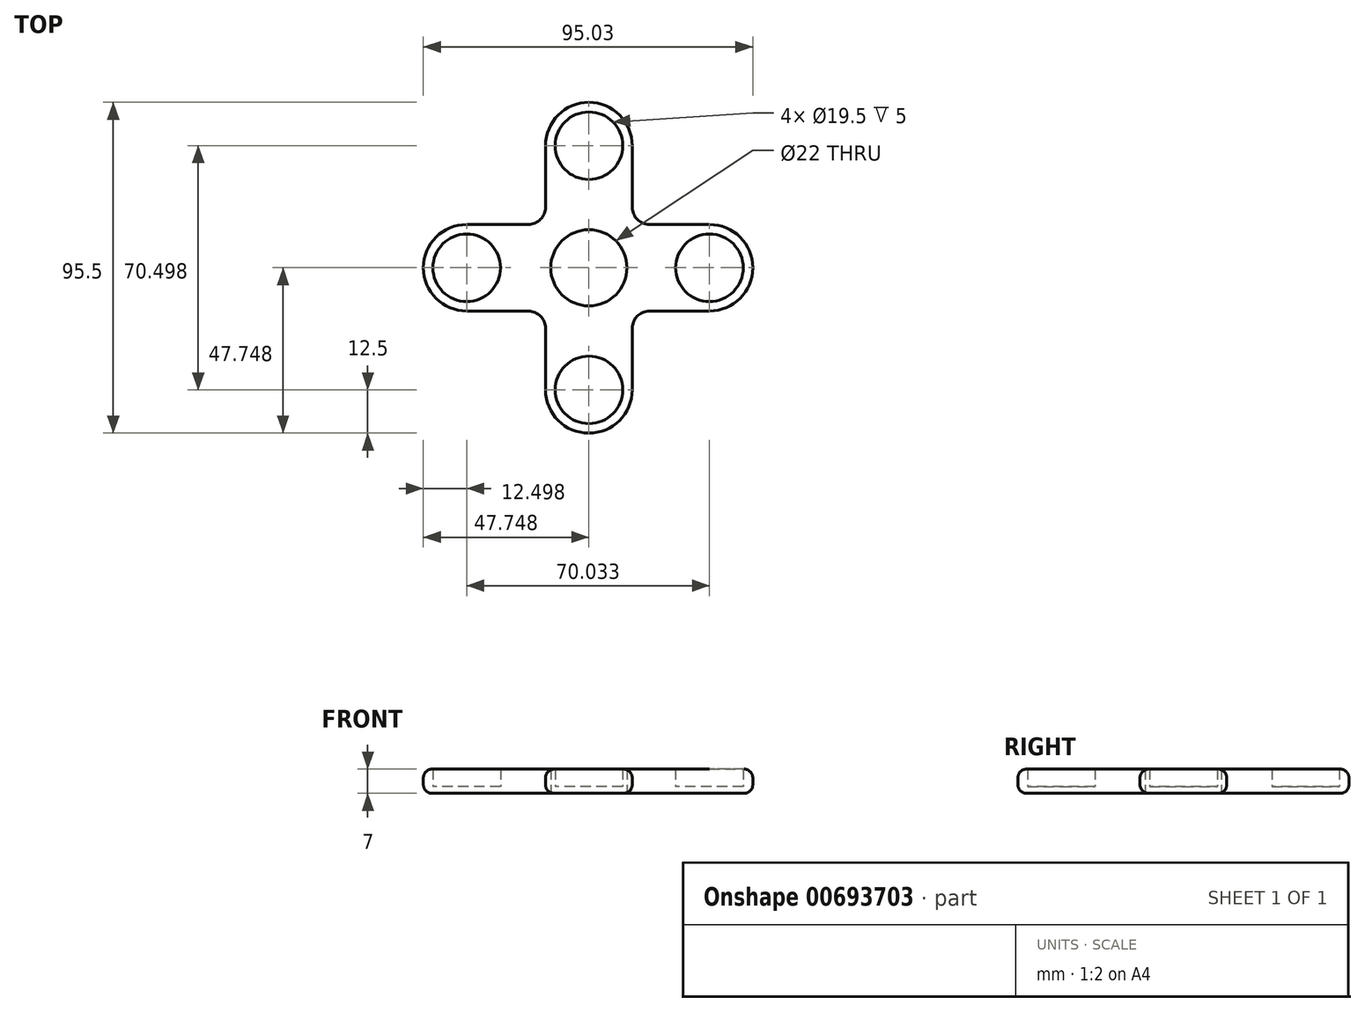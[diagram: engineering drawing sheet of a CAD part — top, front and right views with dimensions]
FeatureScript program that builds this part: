
annotation { "Feature Type Name" : "Feature", "Feature Type Description" : "" }
export const myFeature = defineFeature(function(context is Context, id is Id, definition is map)
    precondition{}
    {
        {
            var Q0;
            Q0=qCreatedBy(makeId("Top.planeOp"),FACE);
            var sketch = newSketch(context, id + "F0", { "sketchPlane" : qUnion([Q0])});
            skCircle(sketch, "E0", {"center": v(-111.62, 35.25) * mm, "radius": 11 * mm});
            skCircle(sketch, "E1", {"center": v(-111.6, 0) * mm, "radius": 9.75 * mm});
            skCircle(sketch, "E2", {"center": v(-111.62, 70.5) * mm, "radius": 9.75 * mm});
            skCircle(sketch, "E3", {"center": v(-76.84, 35.25) * mm, "radius": 9.75 * mm});
            skCircle(sketch, "E4", {"center": v(-146.87, 35.25) * mm, "radius": 9.75 * mm});
            skCircle(sketch, "E5", {"center": v(-111.62, 70.5) * mm, "radius": 12.5 * mm});
            skCircle(sketch, "E6", {"center": v(-146.87, 35.25) * mm, "radius": 12.5 * mm});
            skCircle(sketch, "E7", {"center": v(-111.62, 0) * mm, "radius": 12.5 * mm});
            skCircle(sketch, "E8", {"center": v(-76.84, 35.25) * mm, "radius": 12.5 * mm});
            skLineSegment(sketch, "E9.left", {"start": v(-124.12, 17.75) * mm, "end": v(-124.12, 0) * mm});
            skLineSegment(sketch, "E9.right", {"start": v(-99.12, 70.5) * mm, "end": v(-99.12, 52.75) * mm});
            skLineSegment(sketch, "E10.top", {"start": v(-94.12, 47.75) * mm, "end": v(-76.84, 47.75) * mm});
            skArc(sketch, "E11.filletArc", {"start": v(-99.12, 52.75) * mm, "mid": v(-97.66, 49.21) * mm, "end": v(-94.12, 47.75) * mm});
            skLineSegment(sketch, "E12", {"start": v(-146.87, 47.75) * mm, "end": v(-129.12, 47.75) * mm});
            skLineSegment(sketch, "E13", {"start": v(-124.12, 22.75) * mm, "end": v(-124.12, 0) * mm});
            skLineSegment(sketch, "E14", {"start": v(-99.12, 0) * mm, "end": v(-99.12, 17.75) * mm});
            skLineSegment(sketch, "E15", {"start": v(-94.12, 22.75) * mm, "end": v(-76.84, 22.75) * mm});
            skPoint(sketch, "E16.visualSharp", {"position": v(-99.12, 22.75) * mm});
            skArc(sketch, "E16.filletArc", {"start": v(-94.12, 22.75) * mm, "mid": v(-97.66, 21.28) * mm, "end": v(-99.12, 17.75) * mm});
            skArc(sketch, "E17.filletArc", {"start": v(-124.12, 17.75) * mm, "mid": v(-125.59, 21.28) * mm, "end": v(-129.12, 22.75) * mm});
            skLineSegment(sketch, "E18", {"start": v(-124.12, 70.5) * mm, "end": v(-124.12, 52.75) * mm});
            skPoint(sketch, "E19.visualSharp", {"position": v(-124.12, 47.75) * mm});
            skArc(sketch, "E19.filletArc", {"start": v(-129.12, 47.75) * mm, "mid": v(-125.59, 49.21) * mm, "end": v(-124.12, 52.75) * mm});
            skLineSegment(sketch, "E20", {"start": v(-129.12, 22.75) * mm, "end": v(-146.87, 22.75) * mm});
            skSolve(sketch);
        }
        {
            var Q0;
            Q0=makeQuery(id+"F0.imprint","IMPRINT",FACE,{"disambiguationData":[TD([[makeQuery(id+"F0.imprint","IMPRINT",EDGE,{"derivedFrom":sQuery(id+"F0.wireOp",EDGE,"E1")}),-1.0]])]});
            var Q1;
            Q1=makeQuery(id+"F0.imprint","IMPRINT",FACE,{"disambiguationData":[TD([[makeQuery(id+"F0.imprint","IMPRINT",EDGE,{"derivedFrom":sQuery(id+"F0.wireOp",EDGE,"E2")}),-1.0]])]});
            var Q2;
            Q2=makeQuery(id+"F0.imprint","IMPRINT",FACE,{"disambiguationData":[TD([[makeQuery(id+"F0.imprint","IMPRINT",EDGE,{"derivedFrom":sQuery(id+"F0.wireOp",EDGE,"E3")}),-1.0]])]});
            var Q3;
            Q3=makeQuery(id+"F0.imprint","IMPRINT",FACE,{"disambiguationData":[TD([[makeQuery(id+"F0.imprint","IMPRINT",EDGE,{"derivedFrom":sQuery(id+"F0.wireOp",EDGE,"E0")}),-1.0]])]});
            var Q4;
            Q4=makeQuery(id+"F0.imprint","IMPRINT",FACE,{"disambiguationData":[TD([[makeQuery(id+"F0.imprint","IMPRINT",EDGE,{"derivedFrom":sQuery(id+"F0.wireOp",EDGE,"E4")}),-1.0]])]});
            extrude(context, id + "F1", {"entities" : qUnion([Q0, Q1, Q2, Q3, Q4]), "depth" : 7 * mm, "offsetDistance" : 25 * mm});
        }
        {
            var Q0;
            Q0=makeQuery(id+"F1.opExtrude","CAP_EDGE",EDGE,{"disambiguationData":[OSD([sQuery(id+"F0.wireOp",EDGE,"E18")])],"isStart":false});
            var Q1;
            Q1=makeQuery(id+"F1.opExtrude","CAP_EDGE",EDGE,{"disambiguationData":[OSD([sQuery(id+"F0.wireOp",EDGE,"E19.filletArc")])],"isStart":false});
            var Q2;
            Q2=makeQuery(id+"F1.opExtrude","CAP_EDGE",EDGE,{"disambiguationData":[OSD([sQuery(id+"F0.wireOp",EDGE,"E20")])],"isStart":true});
            var Q3;
            Q3=makeQuery(id+"F1.opExtrude","CAP_EDGE",EDGE,{"disambiguationData":[OSD([sQuery(id+"F0.wireOp",EDGE,"E17.filletArc")])],"isStart":true});
            var Q4;
            Q4=makeQuery(id+"F1.opExtrude","CAP_EDGE",EDGE,{"disambiguationData":[OSD([sQuery(id+"F0.wireOp",EDGE,"E13")])],"isStart":true});
            var Q5;
            Q5=makeQuery(id+"F1.opExtrude","CAP_EDGE",EDGE,{"disambiguationData":[OSD([sQuery(id+"F0.wireOp",EDGE,"E7")])],"isStart":false});
            var Q6;
            Q6=makeQuery(id+"F1.opExtrude","CAP_EDGE",EDGE,{"disambiguationData":[OSD([sQuery(id+"F0.wireOp",EDGE,"E14")])],"isStart":true});
            var Q7;
            Q7=makeQuery(id+"F1.opExtrude","CAP_EDGE",EDGE,{"disambiguationData":[OSD([sQuery(id+"F0.wireOp",EDGE,"E7")])],"isStart":true});
            var Q8;
            Q8=makeQuery(id+"F1.opExtrude","CAP_EDGE",EDGE,{"disambiguationData":[OSD([sQuery(id+"F0.wireOp",EDGE,"E5")])],"isStart":false});
            var Q9;
            Q9=makeQuery(id+"F1.opExtrude","CAP_EDGE",EDGE,{"disambiguationData":[OSD([sQuery(id+"F0.wireOp",EDGE,"E9.right")])],"isStart":false});
            var Q10;
            Q10=makeQuery(id+"F1.opExtrude","CAP_EDGE",EDGE,{"disambiguationData":[OSD([sQuery(id+"F0.wireOp",EDGE,"E11.filletArc")])],"isStart":false});
            var Q11;
            Q11=makeQuery(id+"F1.opExtrude","CAP_EDGE",EDGE,{"disambiguationData":[OSD([sQuery(id+"F0.wireOp",EDGE,"E10.top")])],"isStart":false});
            var Q12;
            Q12=makeQuery(id+"F1.opExtrude","CAP_EDGE",EDGE,{"disambiguationData":[OSD([sQuery(id+"F0.wireOp",EDGE,"E8")])],"isStart":false});
            var Q13;
            Q13=makeQuery(id+"F1.opExtrude","CAP_EDGE",EDGE,{"disambiguationData":[OSD([sQuery(id+"F0.wireOp",EDGE,"E15")])],"isStart":false});
            var Q14;
            Q14=makeQuery(id+"F1.opExtrude","CAP_EDGE",EDGE,{"disambiguationData":[OSD([sQuery(id+"F0.wireOp",EDGE,"E16.filletArc")])],"isStart":false});
            var Q15;
            Q15=makeQuery(id+"F1.opExtrude","CAP_EDGE",EDGE,{"disambiguationData":[OSD([sQuery(id+"F0.wireOp",EDGE,"E14")])],"isStart":false});
            var Q16;
            Q16=makeQuery(id+"F1.opExtrude","CAP_EDGE",EDGE,{"disambiguationData":[OSD([sQuery(id+"F0.wireOp",EDGE,"E6")])],"isStart":false});
            var Q17;
            Q17=makeQuery(id+"F1.opExtrude","CAP_EDGE",EDGE,{"disambiguationData":[OSD([sQuery(id+"F0.wireOp",EDGE,"E12")])],"isStart":false});
            var Q18;
            Q18=makeQuery(id+"F1.opExtrude","CAP_EDGE",EDGE,{"disambiguationData":[OSD([sQuery(id+"F0.wireOp",EDGE,"E13")])],"isStart":false});
            var Q19;
            Q19=makeQuery(id+"F1.opExtrude","CAP_EDGE",EDGE,{"disambiguationData":[OSD([sQuery(id+"F0.wireOp",EDGE,"E17.filletArc")])],"isStart":false});
            var Q20;
            Q20=makeQuery(id+"F1.opExtrude","CAP_EDGE",EDGE,{"disambiguationData":[OSD([sQuery(id+"F0.wireOp",EDGE,"E20")])],"isStart":false});
            var Q21;
            Q21=makeQuery(id+"F1.opExtrude","CAP_EDGE",EDGE,{"disambiguationData":[OSD([sQuery(id+"F0.wireOp",EDGE,"E16.filletArc")])],"isStart":true});
            var Q22;
            Q22=makeQuery(id+"F1.opExtrude","CAP_EDGE",EDGE,{"disambiguationData":[OSD([sQuery(id+"F0.wireOp",EDGE,"E15")])],"isStart":true});
            var Q23;
            Q23=makeQuery(id+"F1.opExtrude","CAP_EDGE",EDGE,{"disambiguationData":[OSD([sQuery(id+"F0.wireOp",EDGE,"E8")])],"isStart":true});
            var Q24;
            Q24=makeQuery(id+"F1.opExtrude","CAP_EDGE",EDGE,{"disambiguationData":[OSD([sQuery(id+"F0.wireOp",EDGE,"E10.top")])],"isStart":true});
            var Q25;
            Q25=makeQuery(id+"F1.opExtrude","CAP_EDGE",EDGE,{"disambiguationData":[OSD([sQuery(id+"F0.wireOp",EDGE,"E5")])],"isStart":true});
            var Q26;
            Q26=makeQuery(id+"F1.opExtrude","CAP_EDGE",EDGE,{"disambiguationData":[OSD([sQuery(id+"F0.wireOp",EDGE,"E11.filletArc")])],"isStart":true});
            var Q27;
            Q27=makeQuery(id+"F1.opExtrude","CAP_EDGE",EDGE,{"disambiguationData":[OSD([sQuery(id+"F0.wireOp",EDGE,"E9.right")])],"isStart":true});
            var Q28;
            Q28=makeQuery(id+"F1.opExtrude","CAP_EDGE",EDGE,{"disambiguationData":[OSD([sQuery(id+"F0.wireOp",EDGE,"E18")])],"isStart":true});
            var Q29;
            Q29=makeQuery(id+"F1.opExtrude","CAP_EDGE",EDGE,{"disambiguationData":[OSD([sQuery(id+"F0.wireOp",EDGE,"E19.filletArc")])],"isStart":true});
            var Q30;
            Q30=makeQuery(id+"F1.opExtrude","CAP_EDGE",EDGE,{"disambiguationData":[OSD([sQuery(id+"F0.wireOp",EDGE,"E12")])],"isStart":true});
            var Q31;
            Q31=makeQuery(id+"F1.opExtrude","CAP_EDGE",EDGE,{"disambiguationData":[OSD([sQuery(id+"F0.wireOp",EDGE,"E6")])],"isStart":true});
            fillet(context, id + "F2", {"entities" : qUnion([Q0, Q1, Q2, Q3, Q4, Q5, Q6, Q7, Q8, Q9, Q10, Q11, Q12, Q13, Q14, Q15, Q16, Q17, Q18, Q19, Q20, Q21, Q22, Q23, Q24, Q25, Q26, Q27, Q28, Q29, Q30, Q31]), "radius" : 2.5 * mm, "tangentPropagation" : true, "allowEdgeOverflow" : false});
        }
        {
            var Q0;
            Q0=makeQuery(id+"F0.imprint","IMPRINT",FACE,{"disambiguationData":[TD([[makeQuery(id+"F0.imprint","IMPRINT",EDGE,{"derivedFrom":sQuery(id+"F0.wireOp",EDGE,"E3")}),1.0]])]});
            var Q1;
            Q1=makeQuery(id+"F0.imprint","IMPRINT",FACE,{"disambiguationData":[TD([[makeQuery(id+"F0.imprint","IMPRINT",EDGE,{"derivedFrom":sQuery(id+"F0.wireOp",EDGE,"E2")}),1.0]])]});
            var Q2;
            Q2=makeQuery(id+"F0.imprint","IMPRINT",FACE,{"disambiguationData":[TD([[makeQuery(id+"F0.imprint","IMPRINT",EDGE,{"derivedFrom":sQuery(id+"F0.wireOp",EDGE,"E4")}),1.0]])]});
            var Q3;
            Q3=makeQuery(id+"F0.imprint","IMPRINT",FACE,{"disambiguationData":[TD([[makeQuery(id+"F0.imprint","IMPRINT",EDGE,{"derivedFrom":sQuery(id+"F0.wireOp",EDGE,"E1")}),1.0]])]});
            extrude(context, id + "F3", {"entities" : qUnion([Q0, Q1, Q2, Q3]), "operationType" : NewBodyOperationType.ADD, "depth" : 2 * mm, "offsetDistance" : 25 * mm});
        }
    });
